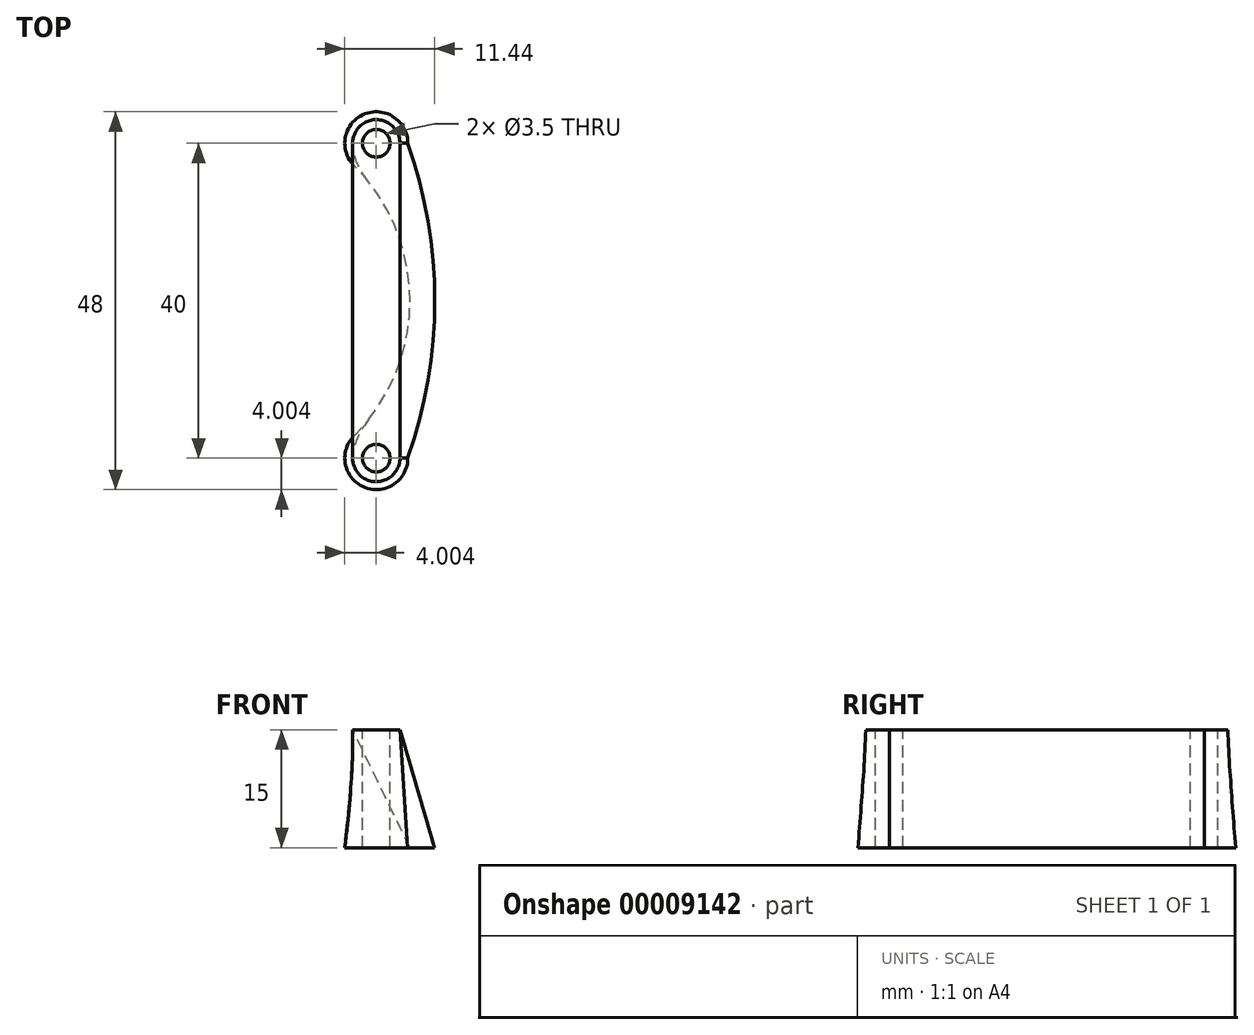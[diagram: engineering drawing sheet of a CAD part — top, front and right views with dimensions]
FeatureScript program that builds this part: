
annotation { "Feature Type Name" : "Feature", "Feature Type Description" : "" }
export const myFeature = defineFeature(function(context is Context, id is Id, definition is map)
    precondition{}
    {
        {
            var Q0;
            Q0=qCreatedBy(makeId("Top.planeOp"),FACE);
            var sketch = newSketch(context, id + "F0", { "sketchPlane" : qUnion([Q0])});
            skLineSegment(sketch, "E0.bottom", {"start": v(-6.5, 21.15) * mm, "end": v(30.5, 21.15) * mm});
            skLineSegment(sketch, "E0.top", {"start": v(-6.5, -13.85) * mm, "end": v(9.5, -13.85) * mm});
            skLineSegment(sketch, "E0.left", {"start": v(-6.5, 21.15) * mm, "end": v(-6.5, -13.85) * mm});
            skLineSegment(sketch, "E0.right", {"start": v(30.5, 21.15) * mm, "end": v(30.5, -4.35) * mm});
            skCircle(sketch, "E1", {"center": v(-9.5, 18.15) * mm, "radius": 1.75 * mm, "construction": true});
            skArc(sketch, "E2", {"start": v(-9.5, 21.15) * mm, "mid": v(-11.63, 20.28) * mm, "end": v(-12.5, 18.15) * mm});
            skCircle(sketch, "E3", {"center": v(-9.5, -21.85) * mm, "radius": 1.75 * mm, "construction": true});
            skArc(sketch, "E4", {"start": v(-12.5, -21.85) * mm, "mid": v(-9.5, -24.85) * mm, "end": v(-6.5, -21.85) * mm});
            skLineSegment(sketch, "E5", {"start": v(-6.5, 21.15) * mm, "end": v(-9.5, 21.15) * mm});
            skLineSegment(sketch, "E6", {"start": v(-12.5, 18.15) * mm, "end": v(-12.5, -21.85) * mm});
            skLineSegment(sketch, "E7", {"start": v(-6.5, -21.85) * mm, "end": v(-6.5, -13.85) * mm});
            skLineSegment(sketch, "E8", {"start": v(30.5, -4.35) * mm, "end": v(9.5, -4.35) * mm});
            skLineSegment(sketch, "E9", {"start": v(9.5, -4.35) * mm, "end": v(9.5, -13.85) * mm});
            skLineSegment(sketch, "E10", {"start": v(-12.5, -21.85) * mm, "end": v(-12.5, -24.85) * mm, "construction": true});
            skLineSegment(sketch, "E11", {"start": v(-12.5, -24.85) * mm, "end": v(-6.5, -24.85) * mm, "construction": true});
            skLineSegment(sketch, "E12", {"start": v(-6.5, -24.85) * mm, "end": v(-6.5, -21.85) * mm, "construction": true});
            skSolve(sketch);
        }
        {
            var Q0;
            Q0=qCreatedBy(makeId("Top.planeOp"),FACE);
            cPlane(context, id + "F1", {"entities" : qUnion([Q0]), "cplaneType" : CPlaneType.OFFSET, "offset" : 15 * mm, "oppositeDirection" : true, "width" : 150 * mm, "height" : 150 * mm});
        }
        {
            var Q0;
            Q0=qCreatedBy(makeId("Top.planeOp"),FACE);
            var sketch = newSketch(context, id + "F2", { "sketchPlane" : qUnion([Q0])});
            skLineSegment(sketch, "E13.bottom", {"start": v(46.15, 21.15) * mm, "end": v(52.15, 21.15) * mm, "construction": true});
            skLineSegment(sketch, "E13.top", {"start": v(46.15, -24.85) * mm, "end": v(52.15, -24.85) * mm, "construction": true});
            skLineSegment(sketch, "E13.left", {"start": v(46.15, 21.15) * mm, "end": v(46.15, -24.85) * mm, "construction": true});
            skCircle(sketch, "E14", {"center": v(49.15, 18.15) * mm, "radius": 1.75 * mm, "construction": true});
            skCircle(sketch, "E15", {"center": v(49.15, -21.85) * mm, "radius": 1.75 * mm, "construction": true});
            skLineSegment(sketch, "E16", {"start": v(49.15, 21.15) * mm, "end": v(49.15, -24.85) * mm, "construction": true});
            skLineSegment(sketch, "E17", {"start": v(52.15, 21.15) * mm, "end": v(52.15, -24.85) * mm, "construction": true});
            skLineSegment(sketch, "E18", {"start": v(46.15, -21.85) * mm, "end": v(52.15, -21.85) * mm, "construction": true});
            skLineSegment(sketch, "E19", {"start": v(52.15, 18.15) * mm, "end": v(46.15, 18.15) * mm, "construction": true});
            skArc(sketch, "E20", {"start": v(46.15, -21.85) * mm, "mid": v(49.15, -24.85) * mm, "end": v(52.15, -21.85) * mm});
            skArc(sketch, "E21", {"start": v(52.15, 18.15) * mm, "mid": v(49.15, 21.15) * mm, "end": v(46.15, 18.15) * mm});
            skLineSegment(sketch, "E22", {"start": v(46.15, 18.15) * mm, "end": v(46.15, -21.85) * mm});
            skLineSegment(sketch, "E23", {"start": v(52.15, 18.15) * mm, "end": v(52.15, -21.85) * mm});
            skSolve(sketch);
        }
        {
            var Q0;
            Q0=qCreatedBy(id+"F1.planeOp",FACE);
            var sketch = newSketch(context, id + "F3", { "sketchPlane" : qUnion([Q0])});
            skLineSegment(sketch, "E24.0.0", {"start": v(46.15, 18.15) * mm, "end": v(46.15, -21.85) * mm, "construction": true});
            skArc(sketch, "E24.0.1", {"start": v(46.15, -21.85) * mm, "mid": v(49.15, -24.85) * mm, "end": v(52.15, -21.85) * mm, "construction": true});
            skLineSegment(sketch, "E24.0.2", {"start": v(52.15, -21.85) * mm, "end": v(52.15, 18.15) * mm, "construction": true});
            skArc(sketch, "E24.0.3", {"start": v(52.15, 18.15) * mm, "mid": v(49.15, 21.15) * mm, "end": v(46.15, 18.15) * mm, "construction": true});
            skCircle(sketch, "E25", {"center": v(49.15, 18.15) * mm, "radius": 4 * mm, "construction": true});
            skCircle(sketch, "E26", {"center": v(49.15, -21.85) * mm, "radius": 4 * mm, "construction": true});
            skLineSegment(sketch, "E27.bottom", {"start": v(49.15, 18.15) * mm, "end": v(9.15, 18.15) * mm, "construction": true});
            skLineSegment(sketch, "E27.top", {"start": v(49.15, -21.85) * mm, "end": v(9.15, -21.85) * mm, "construction": true});
            skLineSegment(sketch, "E27.left", {"start": v(49.15, 18.15) * mm, "end": v(49.15, -21.85) * mm, "construction": true});
            skLineSegment(sketch, "E27.right", {"start": v(9.15, 18.15) * mm, "end": v(9.15, -21.85) * mm, "construction": true});
            skLineSegment(sketch, "E28", {"start": v(29.15, 18.15) * mm, "end": v(29.15, -21.85) * mm, "construction": true});
            skArc(sketch, "E29", {"start": v(46.33, -19.02) * mm, "mid": v(53.44, -1.85) * mm, "end": v(46.33, 15.33) * mm});
            skArc(sketch, "E30", {"start": v(46.33, -19.02) * mm, "mid": v(47.62, -25.54) * mm, "end": v(53.15, -21.85) * mm});
            skArc(sketch, "E31", {"start": v(53.15, 18.15) * mm, "mid": v(47.62, 21.85) * mm, "end": v(46.33, 15.33) * mm});
            skArc(sketch, "E32", {"start": v(53.15, -21.85) * mm, "mid": v(56.59, -1.85) * mm, "end": v(53.15, 18.15) * mm});
            skSolve(sketch);
        }
        {
            var Q0;
            Q0=makeQuery(id+"F3.imprint","IMPRINT",FACE,{"disambiguationData":[TD([[makeQuery(id+"F3.imprint","IMPRINT",EDGE,{"derivedFrom":sQuery(id+"F3.wireOp",EDGE,"E29")}),-1.0]])]});
            var Q1;
            Q1=makeQuery(id+"F2.imprint","IMPRINT",FACE,{"disambiguationData":[TD([[makeQuery(id+"F2.imprint","IMPRINT",EDGE,{"derivedFrom":sQuery(id+"F2.wireOp",EDGE,"E20")}),1.0]])]});
            loft(context, id + "F4", {"sheetProfilesArray" : [{ "sheetProfileEntities" : qUnion([Q0]) }, { "sheetProfileEntities" : qUnion([Q1]) }]});
        }
        {
            var Q0;
            Q0=qCreatedBy(makeId("Top.planeOp"),FACE);
            var sketch = newSketch(context, id + "F5", { "sketchPlane" : qUnion([Q0])});
            skCircle(sketch, "E33.0", {"center": v(49.15, 18.15) * mm, "radius": 1.75 * mm});
            skCircle(sketch, "E34.0", {"center": v(49.15, -21.85) * mm, "radius": 1.75 * mm});
            skSolve(sketch);
        }
        {
            var Q0;
            Q0=makeQuery(id+"F5.imprint","IMPRINT",FACE,{"disambiguationData":[TD([[makeQuery(id+"F5.imprint","IMPRINT",EDGE,{"derivedFrom":sQuery(id+"F5.wireOp",EDGE,"E33.0")}),1.0]])]});
            var Q1;
            Q1=makeQuery(id+"F5.imprint","IMPRINT",FACE,{"disambiguationData":[TD([[makeQuery(id+"F5.imprint","IMPRINT",EDGE,{"derivedFrom":sQuery(id+"F5.wireOp",EDGE,"E34.0")}),1.0]])]});
            var Q2;
            Q2=makeQuery(id+"F4.opLoft","CAP_FACE",FACE,{"disambiguationData":[OSD([makeQuery(id+"F3.imprint","IMPRINT",FACE,{"disambiguationData":[TD([[makeQuery(id+"F3.imprint","IMPRINT",EDGE,{"derivedFrom":sQuery(id+"F3.wireOp",EDGE,"E29")}),-1.0]])]})])],"isStart":true});
            extrude(context, id + "F6", {"entities" : qUnion([Q0, Q1]), "operationType" : NewBodyOperationType.REMOVE, "endBound" : BoundingType.UP_TO_SURFACE, "oppositeDirection" : true, "endBoundEntityFace" : qUnion([Q2]), "depth" : 25 * mm});
        }
    });
